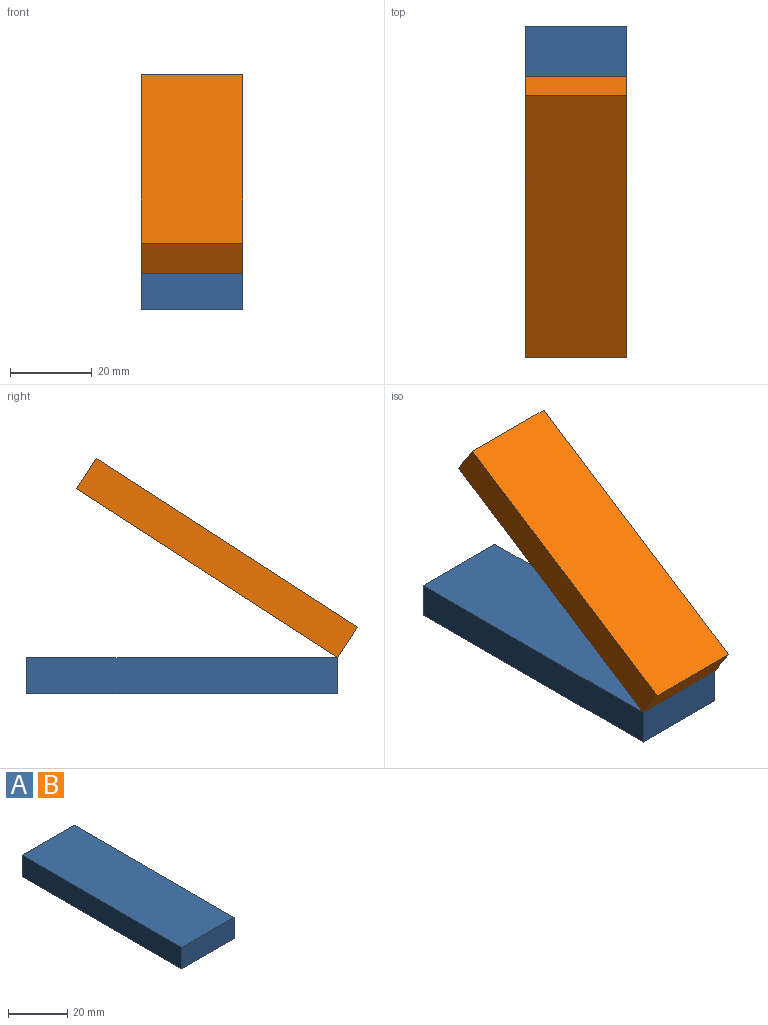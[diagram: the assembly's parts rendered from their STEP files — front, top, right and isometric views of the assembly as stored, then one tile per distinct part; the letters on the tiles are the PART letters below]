
ASSEMBLY  parts=2 mates=1
PART A: 6 faces, bbox 24.8x76.2x8.8 mm
  f0: plane 76.2x8.85mm, normal (-1,0,0), area 674.3mm2, adj f1,f3,f4,f5
  f1: plane 76.2x24.8mm, normal (0,0,-1), area 1889.8mm2, adj f0,f2,f4,f5
  f2: plane 76.2x8.85mm, normal (1,0,0), area 674.3mm2, adj f1,f3,f4,f5
  f3: plane 76.2x24.8mm, normal (0,0,1), area 1889.8mm2, adj f0,f2,f4,f5
  f4: plane 24.8x8.85mm, normal (0,-1,0), area 219.4mm2, adj f0,f1,f2,f3
  f5: plane 24.8x8.85mm, normal (0,1,0), area 219.4mm2, adj f0,f1,f2,f3
PART B: same geometry as A
PLACE A t=(-14.54,76.29,-1.92)mm fixed
PLACE B rot(axis=(1,0,0),32.9deg) t=(-14.54,64.07,48.31)mm
MATE revolute B.f2 <-> A.f2  axis (1,0,0) through (10.26,0.09,6.93)mm
